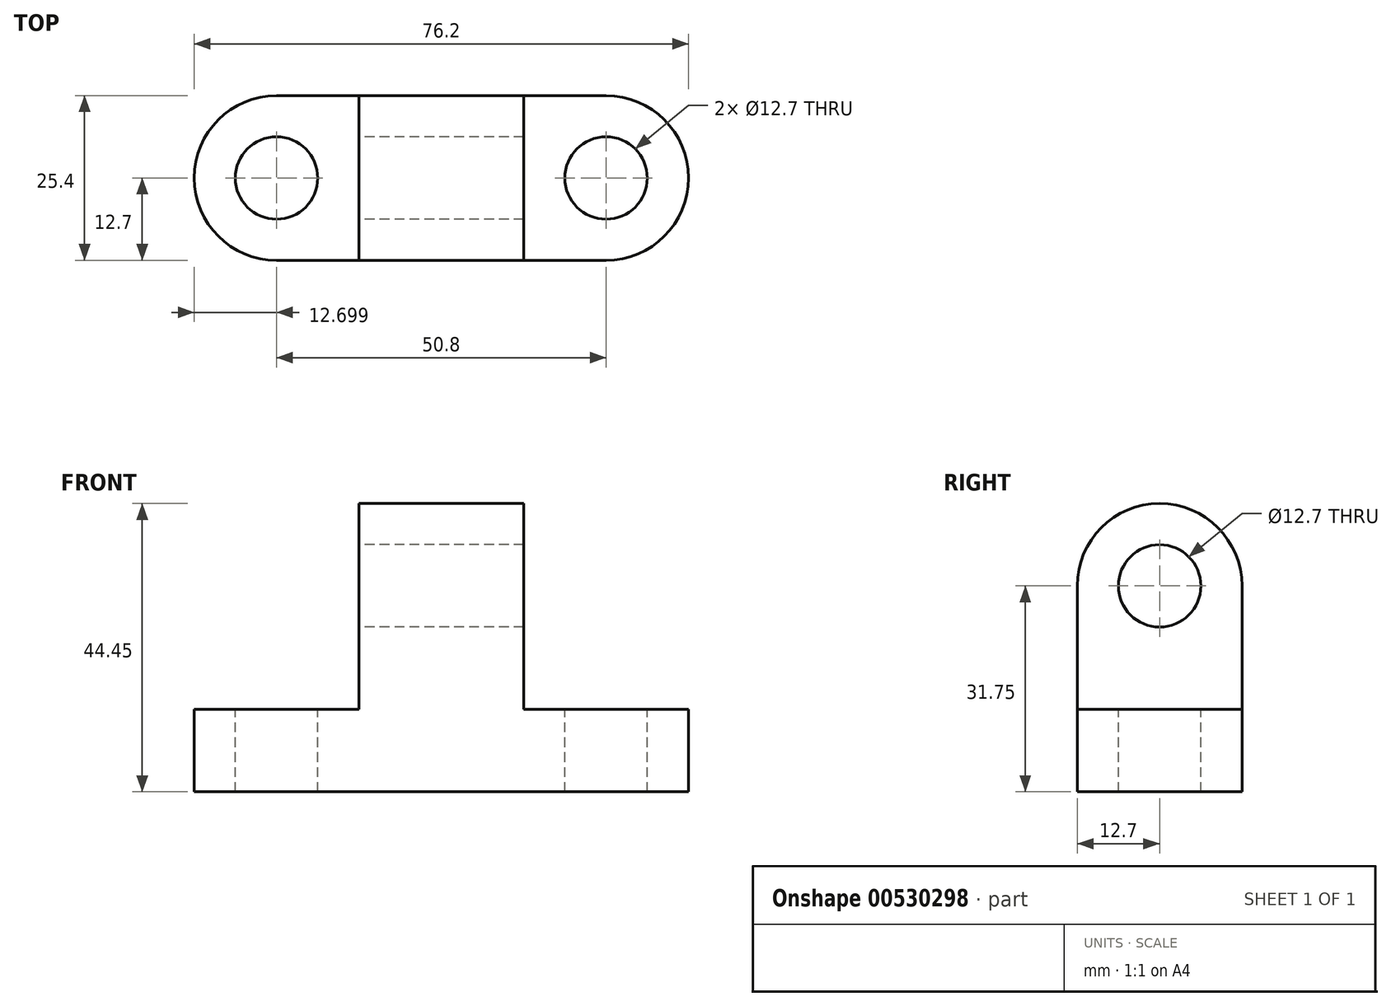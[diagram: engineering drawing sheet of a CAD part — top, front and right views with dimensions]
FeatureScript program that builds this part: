
annotation { "Feature Type Name" : "Feature", "Feature Type Description" : "" }
export const myFeature = defineFeature(function(context is Context, id is Id, definition is map)
    precondition{}
    {
        {
            var Q0;
            Q0=qCreatedBy(makeId("Front.planeOp"),FACE);
            var sketch = newSketch(context, id + "F0", { "sketchPlane" : qUnion([Q0])});
            skLineSegment(sketch, "E0", {"start": v(-40.44, 0) * mm, "end": v(35.76, 0) * mm});
            skLineSegment(sketch, "E1", {"start": v(-40.44, 0) * mm, "end": v(-40.44, 12.7) * mm});
            skLineSegment(sketch, "E2", {"start": v(-40.44, 12.7) * mm, "end": v(-15.04, 12.7) * mm});
            skLineSegment(sketch, "E3", {"start": v(-15.04, 12.7) * mm, "end": v(-15.04, 44.45) * mm});
            skLineSegment(sketch, "E4", {"start": v(10.36, 44.45) * mm, "end": v(10.36, 12.7) * mm});
            skLineSegment(sketch, "E5", {"start": v(10.36, 12.7) * mm, "end": v(35.76, 12.7) * mm});
            skLineSegment(sketch, "E6", {"start": v(35.76, 12.7) * mm, "end": v(35.76, 0) * mm});
            skLineSegment(sketch, "E7", {"start": v(-15.04, 44.45) * mm, "end": v(10.36, 44.45) * mm});
            skSolve(sketch);
        }
        {
            var Q0;
            Q0=makeQuery(id+"F0.imprint","IMPRINT",FACE,{"disambiguationData":[TD([[makeQuery(id+"F0.imprint","IMPRINT",EDGE,{"derivedFrom":sQuery(id+"F0.wireOp",EDGE,"E0")}),1.0]])]});
            extrude(context, id + "F1", {"entities" : qUnion([Q0]), "depth" : 25.4 * mm, "offsetDistance" : 25.4 * mm});
        }
        {
            var Q0;
            Q0=makeQuery(id+"F1.opExtrude","SWEPT_FACE",FACE,{"disambiguationData":[OSD([sQuery(id+"F0.wireOp",EDGE,"E3")])]});
            var sketch = newSketch(context, id + "F2", { "sketchPlane" : qUnion([Q0])});
            skCircle(sketch, "E8", {"center": v(12.7, 31.75) * mm, "radius": 6.35 * mm});
            skPoint(sketch, "E9.endSnap0", {"position": v(25.4, 28.58) * mm});
            skArc(sketch, "E10", {"start": v(25.4, 31.75) * mm, "mid": v(12.7, 44.45) * mm, "end": v(0, 31.75) * mm});
            skSolve(sketch);
        }
        {
            var Q0;
            {var subQ0=sQuery(id+"F2.wireOp",EDGE,"E10");var subQ1=sQuery(id+"F0.wireOp",EDGE,"E3");var subQ2=makeQuery(id+"F1.opExtrude","CAP_EDGE",EDGE,{"disambiguationData":[OSD([subQ1])],"isStart":false});var subQ3=makeQuery(id+"F2.imprint","INTERSECT",VERTEX,{"derivedFrom":[subQ2,subQ0]});Q0=makeQuery(id+"F2.imprint","IMPRINT",FACE,{"disambiguationData":[TD([[makeQuery(id+"F2.imprint","IMPRINT",EDGE,{"disambiguationData":[TD([[subQ3,-1.0]])],"derivedFrom":subQ0}),-1.0]])]});}
            var Q1;
            {var subQ0=sQuery(id+"F2.wireOp",EDGE,"E10");var subQ1=sQuery(id+"F0.wireOp",EDGE,"E3");var subQ2=makeQuery(id+"F1.opExtrude","CAP_EDGE",EDGE,{"disambiguationData":[OSD([subQ1])],"isStart":true});var subQ3=makeQuery(id+"F2.imprint","INTERSECT",VERTEX,{"derivedFrom":[subQ2,subQ0]});Q1=makeQuery(id+"F2.imprint","IMPRINT",FACE,{"disambiguationData":[TD([[makeQuery(id+"F2.imprint","IMPRINT",EDGE,{"disambiguationData":[TD([[subQ3,1.0]])],"derivedFrom":subQ0}),-1.0]])]});}
            var Q2;
            Q2=makeQuery(id+"F2.imprint","IMPRINT",FACE,{"disambiguationData":[TD([[makeQuery(id+"F2.imprint","IMPRINT",EDGE,{"derivedFrom":sQuery(id+"F2.wireOp",EDGE,"E8")}),1.0]])]});
            extrude(context, id + "F3", {"entities" : qUnion([Q0, Q1, Q2]), "operationType" : NewBodyOperationType.REMOVE, "oppositeDirection" : true, "depth" : 25.4 * mm, "offsetDistance" : 25.4 * mm});
        }
        {
            var Q0;
            Q0=makeQuery(id+"F1.opExtrude","SWEPT_FACE",FACE,{"disambiguationData":[OSD([sQuery(id+"F0.wireOp",EDGE,"E2")])]});
            var sketch = newSketch(context, id + "F4", { "sketchPlane" : qUnion([Q0])});
            skCircle(sketch, "E11", {"center": v(-27.74, -12.7) * mm, "radius": 6.35 * mm});
            skArc(sketch, "E12", {"start": v(-27.74, 0) * mm, "mid": v(-40.44, -12.7) * mm, "end": v(-27.74, -25.4) * mm});
            skSolve(sketch);
        }
        {
            var Q0;
            Q0=makeQuery(id+"F4.imprint","IMPRINT",FACE,{"disambiguationData":[TD([[makeQuery(id+"F4.imprint","IMPRINT",EDGE,{"derivedFrom":sQuery(id+"F4.wireOp",EDGE,"E11")}),1.0]])]});
            var Q1;
            {var subQ0=sQuery(id+"F4.wireOp",EDGE,"E12");var subQ1=sQuery(id+"F0.wireOp",EDGE,"E2");var subQ2=makeQuery(id+"F1.opExtrude","CAP_EDGE",EDGE,{"disambiguationData":[OSD([subQ1])],"isStart":true});var subQ3=makeQuery(id+"F4.imprint","INTERSECT",VERTEX,{"derivedFrom":[subQ2,subQ0]});Q1=makeQuery(id+"F4.imprint","IMPRINT",FACE,{"disambiguationData":[TD([[makeQuery(id+"F4.imprint","IMPRINT",EDGE,{"disambiguationData":[TD([[subQ3,-1.0]])],"derivedFrom":subQ0}),-1.0]])]});}
            var Q2;
            {var subQ0=sQuery(id+"F4.wireOp",EDGE,"E12");var subQ1=sQuery(id+"F0.wireOp",EDGE,"E2");var subQ2=makeQuery(id+"F1.opExtrude","CAP_EDGE",EDGE,{"disambiguationData":[OSD([subQ1])],"isStart":false});var subQ3=makeQuery(id+"F4.imprint","INTERSECT",VERTEX,{"derivedFrom":[subQ2,subQ0]});Q2=makeQuery(id+"F4.imprint","IMPRINT",FACE,{"disambiguationData":[TD([[makeQuery(id+"F4.imprint","IMPRINT",EDGE,{"disambiguationData":[TD([[subQ3,1.0]])],"derivedFrom":subQ0}),-1.0]])]});}
            extrude(context, id + "F5", {"entities" : qUnion([Q0, Q1, Q2]), "operationType" : NewBodyOperationType.REMOVE, "endBound" : BoundingType.THROUGH_ALL, "oppositeDirection" : true, "depth" : 25.4 * mm, "offsetDistance" : 25.4 * mm});
        }
        {
            var Q0;
            Q0=makeQuery(id+"F1.opExtrude","SWEPT_FACE",FACE,{"disambiguationData":[OSD([sQuery(id+"F0.wireOp",EDGE,"E5")])]});
            var sketch = newSketch(context, id + "F6", { "sketchPlane" : qUnion([Q0])});
            skCircle(sketch, "E13", {"center": v(23.06, -12.7) * mm, "radius": 6.35 * mm});
            skPoint(sketch, "E13.centerSnap0", {"position": v(23.06, 0) * mm});
            skArc(sketch, "E14", {"start": v(23.06, -25.4) * mm, "mid": v(35.76, -12.7) * mm, "end": v(23.06, 0) * mm});
            skSolve(sketch);
        }
        {
            var Q0;
            {var subQ0=sQuery(id+"F6.wireOp",EDGE,"E14");var subQ1=sQuery(id+"F0.wireOp",EDGE,"E5");var subQ2=makeQuery(id+"F1.opExtrude","CAP_EDGE",EDGE,{"disambiguationData":[OSD([subQ1])],"isStart":true});var subQ3=makeQuery(id+"F6.imprint","INTERSECT",VERTEX,{"derivedFrom":[subQ2,subQ0]});Q0=makeQuery(id+"F6.imprint","IMPRINT",FACE,{"disambiguationData":[TD([[makeQuery(id+"F6.imprint","IMPRINT",EDGE,{"disambiguationData":[TD([[subQ3,1.0]])],"derivedFrom":subQ0}),-1.0]])]});}
            var Q1;
            {var subQ0=sQuery(id+"F6.wireOp",EDGE,"E14");var subQ1=sQuery(id+"F0.wireOp",EDGE,"E5");var subQ2=makeQuery(id+"F1.opExtrude","CAP_EDGE",EDGE,{"disambiguationData":[OSD([subQ1])],"isStart":false});var subQ3=makeQuery(id+"F6.imprint","INTERSECT",VERTEX,{"derivedFrom":[subQ2,subQ0]});Q1=makeQuery(id+"F6.imprint","IMPRINT",FACE,{"disambiguationData":[TD([[makeQuery(id+"F6.imprint","IMPRINT",EDGE,{"disambiguationData":[TD([[subQ3,-1.0]])],"derivedFrom":subQ0}),-1.0]])]});}
            var Q2;
            Q2=makeQuery(id+"F6.imprint","IMPRINT",FACE,{"disambiguationData":[TD([[makeQuery(id+"F6.imprint","IMPRINT",EDGE,{"derivedFrom":sQuery(id+"F6.wireOp",EDGE,"E13")}),1.0]])]});
            extrude(context, id + "F7", {"entities" : qUnion([Q0, Q1, Q2]), "operationType" : NewBodyOperationType.REMOVE, "endBound" : BoundingType.THROUGH_ALL, "oppositeDirection" : true, "depth" : 25.4 * mm, "offsetDistance" : 25.4 * mm});
        }
    });
